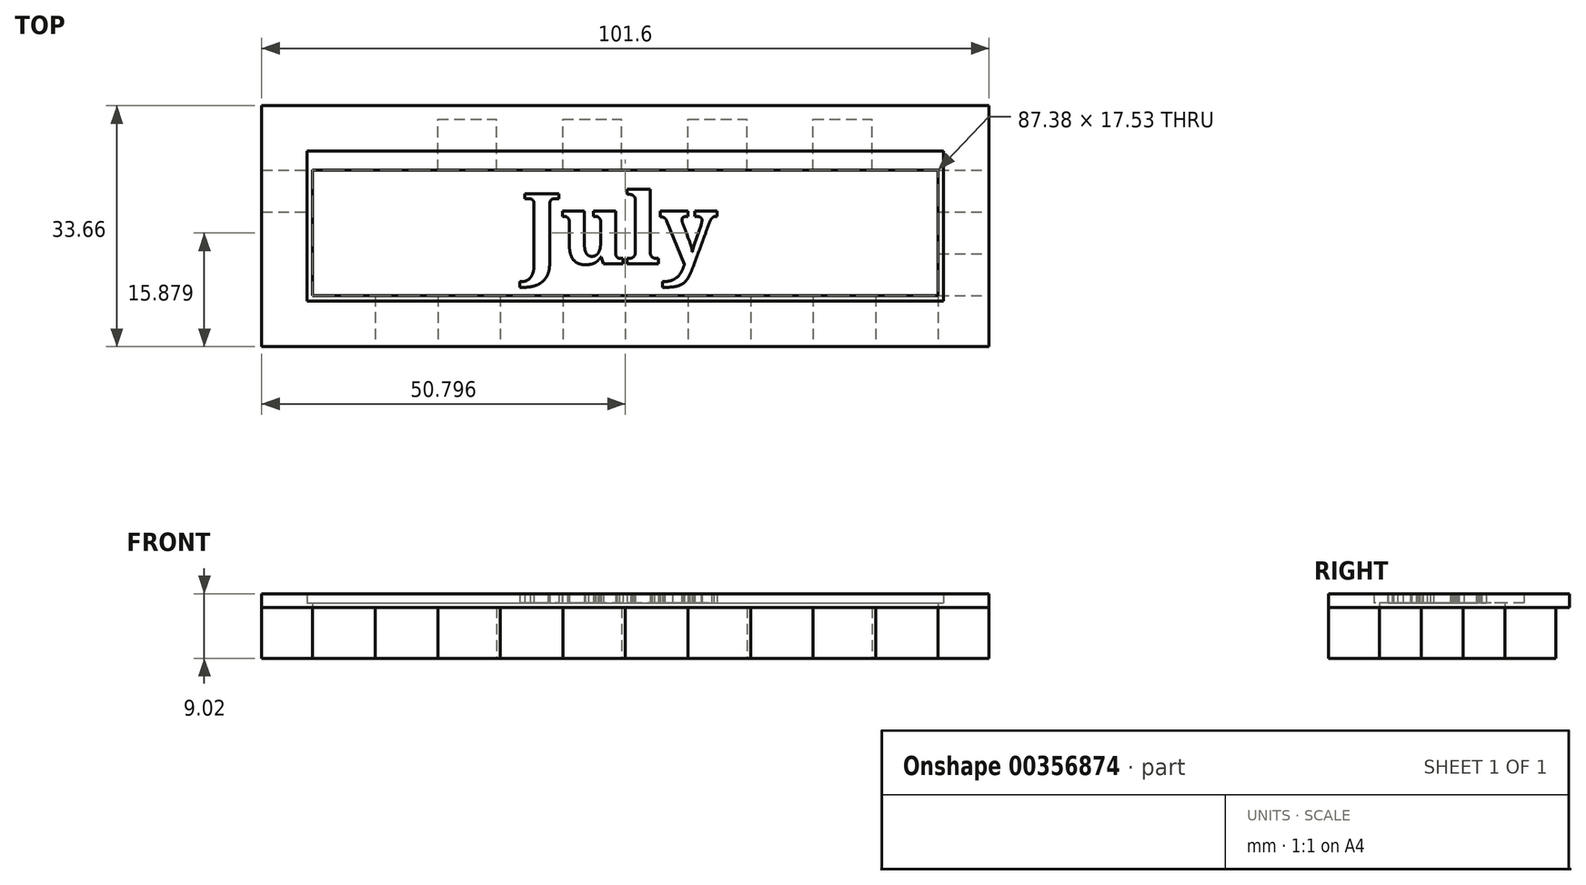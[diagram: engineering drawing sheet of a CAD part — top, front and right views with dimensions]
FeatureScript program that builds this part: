
annotation { "Feature Type Name" : "Feature", "Feature Type Description" : "" }
export const myFeature = defineFeature(function(context is Context, id is Id, definition is map)
    precondition{}
    {
        {
            var Q0;
            Q0=qCreatedBy(makeId("Top.planeOp"),FACE);
            var sketch = newSketch(context, id + "F0", { "sketchPlane" : qUnion([Q0])});
            skLineSegment(sketch, "E0.bottom", {"start": v(-52.12, 11.37) * mm, "end": v(49.48, 11.37) * mm});
            skLineSegment(sketch, "E0.top", {"start": v(-52.12, -20.38) * mm, "end": v(49.48, -20.38) * mm});
            skLineSegment(sketch, "E0.left", {"start": v(-52.12, 11.37) * mm, "end": v(-52.12, -20.38) * mm});
            skLineSegment(sketch, "E0.right", {"start": v(49.48, 11.37) * mm, "end": v(49.48, -20.38) * mm});
            skLineSegment(sketch, "E1.bottom", {"start": v(-52.12, 11.37) * mm, "end": v(-45.01, 11.37) * mm});
            skLineSegment(sketch, "E1.top", {"start": v(-52.12, 4.26) * mm, "end": v(-45.01, 4.26) * mm});
            skLineSegment(sketch, "E1.left", {"start": v(-52.12, 11.37) * mm, "end": v(-52.12, 4.26) * mm});
            skLineSegment(sketch, "E1.right", {"start": v(-45.01, 11.37) * mm, "end": v(-45.01, 4.26) * mm});
            skLineSegment(sketch, "E2.bottom", {"start": v(-45.01, 11.37) * mm, "end": v(-36.78, 11.37) * mm});
            skLineSegment(sketch, "E2.top", {"start": v(-45.01, 4.26) * mm, "end": v(-36.78, 4.26) * mm});
            skLineSegment(sketch, "E2.right", {"start": v(-36.78, 11.37) * mm, "end": v(-36.78, 4.26) * mm});
            skLineSegment(sketch, "E3.bottom", {"start": v(-36.78, 4.26) * mm, "end": v(-27.54, 4.26) * mm});
            skLineSegment(sketch, "E3.top", {"start": v(-36.78, 11.37) * mm, "end": v(-27.54, 11.37) * mm});
            skLineSegment(sketch, "E3.left", {"start": v(-36.78, 4.26) * mm, "end": v(-36.78, 11.37) * mm});
            skLineSegment(sketch, "E3.right", {"start": v(-27.54, 4.26) * mm, "end": v(-27.54, 11.37) * mm});
            skLineSegment(sketch, "E4.bottom", {"start": v(-27.54, 4.26) * mm, "end": v(-19.3, 4.26) * mm});
            skLineSegment(sketch, "E4.top", {"start": v(-27.54, 11.37) * mm, "end": v(-19.3, 11.37) * mm});
            skLineSegment(sketch, "E4.right", {"start": v(-19.3, 4.26) * mm, "end": v(-19.3, 11.37) * mm});
            skLineSegment(sketch, "E5.bottom", {"start": v(-19.3, 4.26) * mm, "end": v(-10.06, 4.26) * mm});
            skLineSegment(sketch, "E5.top", {"start": v(-19.3, 11.37) * mm, "end": v(-10.06, 11.37) * mm});
            skLineSegment(sketch, "E5.right", {"start": v(-10.06, 4.26) * mm, "end": v(-10.06, 11.37) * mm});
            skLineSegment(sketch, "E6.bottom", {"start": v(-10.06, 4.26) * mm, "end": v(-10.06, 4.26) * mm});
            skLineSegment(sketch, "E6.top", {"start": v(-10.06, 11.37) * mm, "end": v(-10.06, 11.37) * mm});
            skLineSegment(sketch, "E7.bottom", {"start": v(-10.06, 4.26) * mm, "end": v(-1.83, 4.26) * mm});
            skLineSegment(sketch, "E7.top", {"start": v(-10.06, 11.37) * mm, "end": v(-1.83, 11.37) * mm});
            skLineSegment(sketch, "E7.right", {"start": v(-1.83, 4.26) * mm, "end": v(-1.83, 11.37) * mm});
            skLineSegment(sketch, "E8.bottom", {"start": v(-1.83, 4.26) * mm, "end": v(7.41, 4.26) * mm});
            skLineSegment(sketch, "E8.top", {"start": v(-1.83, 11.37) * mm, "end": v(7.41, 11.37) * mm});
            skLineSegment(sketch, "E8.right", {"start": v(7.41, 4.26) * mm, "end": v(7.41, 11.37) * mm});
            skLineSegment(sketch, "E9.bottom", {"start": v(7.41, 4.26) * mm, "end": v(15.64, 4.26) * mm});
            skLineSegment(sketch, "E9.top", {"start": v(7.41, 11.37) * mm, "end": v(15.64, 11.37) * mm});
            skLineSegment(sketch, "E9.right", {"start": v(15.64, 4.26) * mm, "end": v(15.64, 11.37) * mm});
            skLineSegment(sketch, "E10.bottom", {"start": v(15.64, 4.26) * mm, "end": v(24.89, 4.26) * mm});
            skLineSegment(sketch, "E10.top", {"start": v(15.64, 11.37) * mm, "end": v(24.89, 11.37) * mm});
            skLineSegment(sketch, "E10.right", {"start": v(24.89, 4.26) * mm, "end": v(24.89, 11.37) * mm});
            skLineSegment(sketch, "E11.bottom", {"start": v(24.89, 4.26) * mm, "end": v(24.89, 4.26) * mm});
            skLineSegment(sketch, "E11.top", {"start": v(24.89, 11.37) * mm, "end": v(24.89, 11.37) * mm});
            skLineSegment(sketch, "E12.bottom", {"start": v(24.89, 4.26) * mm, "end": v(33.12, 4.26) * mm});
            skLineSegment(sketch, "E12.top", {"start": v(24.89, 11.37) * mm, "end": v(33.12, 11.37) * mm});
            skLineSegment(sketch, "E12.right", {"start": v(33.12, 4.26) * mm, "end": v(33.12, 11.37) * mm});
            skLineSegment(sketch, "E13.bottom", {"start": v(33.12, 4.26) * mm, "end": v(42.36, 4.26) * mm});
            skLineSegment(sketch, "E13.top", {"start": v(33.12, 11.37) * mm, "end": v(42.36, 11.37) * mm});
            skLineSegment(sketch, "E13.right", {"start": v(42.36, 4.26) * mm, "end": v(42.36, 11.37) * mm});
            skLineSegment(sketch, "E14.bottom", {"start": v(42.36, 4.26) * mm, "end": v(49.48, 4.26) * mm});
            skLineSegment(sketch, "E14.top", {"start": v(42.36, 11.37) * mm, "end": v(49.48, 11.37) * mm});
            skLineSegment(sketch, "E14.right", {"start": v(49.48, 4.26) * mm, "end": v(49.48, 11.37) * mm});
            skLineSegment(sketch, "E15.bottom", {"start": v(-52.12, -20.38) * mm, "end": v(-45.01, -20.38) * mm});
            skLineSegment(sketch, "E15.top", {"start": v(-52.12, -13.26) * mm, "end": v(-45.01, -13.26) * mm});
            skLineSegment(sketch, "E15.left", {"start": v(-52.12, -20.38) * mm, "end": v(-52.12, -13.26) * mm});
            skLineSegment(sketch, "E15.right", {"start": v(-45.01, -20.38) * mm, "end": v(-45.01, -13.26) * mm});
            skLineSegment(sketch, "E16.bottom", {"start": v(-45.01, -13.26) * mm, "end": v(-45.01, -13.26) * mm});
            skLineSegment(sketch, "E16.top", {"start": v(-45.01, -20.38) * mm, "end": v(-45.01, -20.38) * mm});
            skLineSegment(sketch, "E16.left", {"start": v(-45.01, -13.26) * mm, "end": v(-45.01, -20.38) * mm});
            skLineSegment(sketch, "E16.right", {"start": v(-45.01, -13.26) * mm, "end": v(-45.01, -20.38) * mm});
            skLineSegment(sketch, "E17.bottom", {"start": v(-45.01, -13.26) * mm, "end": v(-36.27, -13.26) * mm});
            skLineSegment(sketch, "E17.top", {"start": v(-45.01, -20.38) * mm, "end": v(-36.27, -20.38) * mm});
            skLineSegment(sketch, "E17.right", {"start": v(-36.27, -13.26) * mm, "end": v(-36.27, -20.38) * mm});
            skLineSegment(sketch, "E18.bottom", {"start": v(-36.27, -13.26) * mm, "end": v(-36.27, -13.26) * mm});
            skLineSegment(sketch, "E18.top", {"start": v(-36.27, -20.38) * mm, "end": v(-36.27, -20.38) * mm});
            skLineSegment(sketch, "E19.bottom", {"start": v(-36.27, -13.26) * mm, "end": v(-27.54, -13.26) * mm});
            skLineSegment(sketch, "E19.top", {"start": v(-36.27, -20.38) * mm, "end": v(-27.54, -20.38) * mm});
            skLineSegment(sketch, "E19.right", {"start": v(-27.54, -13.26) * mm, "end": v(-27.54, -20.38) * mm});
            skLineSegment(sketch, "E20.bottom", {"start": v(-27.54, -13.26) * mm, "end": v(-18.8, -13.26) * mm});
            skLineSegment(sketch, "E20.top", {"start": v(-27.54, -20.38) * mm, "end": v(-18.8, -20.38) * mm});
            skLineSegment(sketch, "E20.right", {"start": v(-18.8, -13.26) * mm, "end": v(-18.8, -20.38) * mm});
            skLineSegment(sketch, "E21.bottom", {"start": v(-18.8, -13.26) * mm, "end": v(-10.06, -13.26) * mm});
            skLineSegment(sketch, "E21.top", {"start": v(-18.8, -20.38) * mm, "end": v(-10.06, -20.38) * mm});
            skLineSegment(sketch, "E21.right", {"start": v(-10.06, -13.26) * mm, "end": v(-10.06, -20.38) * mm});
            skLineSegment(sketch, "E22.bottom", {"start": v(-10.06, -13.26) * mm, "end": v(-1.32, -13.26) * mm});
            skLineSegment(sketch, "E22.top", {"start": v(-10.06, -20.38) * mm, "end": v(-1.32, -20.38) * mm});
            skLineSegment(sketch, "E22.right", {"start": v(-1.32, -13.26) * mm, "end": v(-1.32, -20.38) * mm});
            skLineSegment(sketch, "E23.bottom", {"start": v(-1.32, -13.26) * mm, "end": v(7.41, -13.26) * mm});
            skLineSegment(sketch, "E23.top", {"start": v(-1.32, -20.38) * mm, "end": v(7.41, -20.38) * mm});
            skLineSegment(sketch, "E23.right", {"start": v(7.41, -13.26) * mm, "end": v(7.41, -20.38) * mm});
            skLineSegment(sketch, "E24.bottom", {"start": v(7.41, -13.26) * mm, "end": v(16.15, -13.26) * mm});
            skLineSegment(sketch, "E24.top", {"start": v(7.41, -20.38) * mm, "end": v(16.15, -20.38) * mm});
            skLineSegment(sketch, "E24.right", {"start": v(16.15, -13.26) * mm, "end": v(16.15, -20.38) * mm});
            skLineSegment(sketch, "E25.bottom", {"start": v(16.15, -13.26) * mm, "end": v(24.89, -13.26) * mm});
            skLineSegment(sketch, "E25.top", {"start": v(16.15, -20.38) * mm, "end": v(24.89, -20.38) * mm});
            skLineSegment(sketch, "E25.right", {"start": v(24.89, -13.26) * mm, "end": v(24.89, -20.38) * mm});
            skLineSegment(sketch, "E26.bottom", {"start": v(24.89, -13.26) * mm, "end": v(33.63, -13.26) * mm});
            skLineSegment(sketch, "E26.top", {"start": v(24.89, -20.38) * mm, "end": v(33.63, -20.38) * mm});
            skLineSegment(sketch, "E26.right", {"start": v(33.63, -13.26) * mm, "end": v(33.63, -20.38) * mm});
            skLineSegment(sketch, "E27.bottom", {"start": v(33.63, -13.26) * mm, "end": v(42.36, -13.26) * mm});
            skLineSegment(sketch, "E27.top", {"start": v(33.63, -20.38) * mm, "end": v(42.36, -20.38) * mm});
            skLineSegment(sketch, "E27.right", {"start": v(42.36, -13.26) * mm, "end": v(42.36, -20.38) * mm});
            skLineSegment(sketch, "E28.bottom", {"start": v(42.36, -13.26) * mm, "end": v(49.48, -13.26) * mm});
            skLineSegment(sketch, "E28.top", {"start": v(42.36, -20.38) * mm, "end": v(49.48, -20.38) * mm});
            skLineSegment(sketch, "E28.right", {"start": v(49.48, -13.26) * mm, "end": v(49.48, -20.38) * mm});
            skLineSegment(sketch, "E29.top", {"start": v(-52.12, -1.58) * mm, "end": v(-45.01, -1.58) * mm});
            skLineSegment(sketch, "E29.left", {"start": v(-52.12, 4.26) * mm, "end": v(-52.12, -1.58) * mm});
            skLineSegment(sketch, "E29.right", {"start": v(-45.01, 4.26) * mm, "end": v(-45.01, -1.58) * mm});
            skLineSegment(sketch, "E30.top", {"start": v(-52.12, -7.42) * mm, "end": v(-45.01, -7.42) * mm});
            skLineSegment(sketch, "E30.left", {"start": v(-52.12, -1.58) * mm, "end": v(-52.12, -7.42) * mm});
            skLineSegment(sketch, "E30.right", {"start": v(-45.01, -1.58) * mm, "end": v(-45.01, -7.42) * mm});
            skLineSegment(sketch, "E31.bottom", {"start": v(-45.01, -7.42) * mm, "end": v(-52.12, -7.42) * mm});
            skLineSegment(sketch, "E31.top", {"start": v(-45.01, -13.26) * mm, "end": v(-52.12, -13.26) * mm});
            skLineSegment(sketch, "E31.left", {"start": v(-45.01, -7.42) * mm, "end": v(-45.01, -13.26) * mm});
            skLineSegment(sketch, "E31.right", {"start": v(-52.12, -7.42) * mm, "end": v(-52.12, -13.26) * mm});
            skLineSegment(sketch, "E32.top", {"start": v(42.36, -1.58) * mm, "end": v(49.48, -1.58) * mm});
            skLineSegment(sketch, "E32.left", {"start": v(42.36, 4.26) * mm, "end": v(42.36, -1.58) * mm});
            skLineSegment(sketch, "E32.right", {"start": v(49.48, 4.26) * mm, "end": v(49.48, -1.58) * mm});
            skLineSegment(sketch, "E33.top", {"start": v(42.36, -7.42) * mm, "end": v(49.48, -7.42) * mm});
            skLineSegment(sketch, "E33.left", {"start": v(42.36, -1.58) * mm, "end": v(42.36, -7.42) * mm});
            skLineSegment(sketch, "E33.right", {"start": v(49.48, -1.58) * mm, "end": v(49.48, -7.42) * mm});
            skLineSegment(sketch, "E34.left", {"start": v(42.36, -7.42) * mm, "end": v(42.36, -13.26) * mm});
            skLineSegment(sketch, "E34.right", {"start": v(49.48, -7.42) * mm, "end": v(49.48, -13.26) * mm});
            skSolve(sketch);
        }
        {
            var Q0;
            Q0=makeQuery(id+"F0.imprint","IMPRINT",FACE,{"disambiguationData":[TD([[makeQuery(id+"F0.imprint","IMPRINT",EDGE,{"derivedFrom":sQuery(id+"F0.wireOp",EDGE,"E2.top")}),-1.0]])]});
            var Q1;
            Q1=makeQuery(id+"F0.imprint","IMPRINT",FACE,{"disambiguationData":[TD([[makeQuery(id+"F0.imprint","IMPRINT",EDGE,{"derivedFrom":sQuery(id+"F0.wireOp",EDGE,"E2.bottom")}),-1.0]])]});
            var Q2;
            Q2=makeQuery(id+"F0.imprint","IMPRINT",FACE,{"disambiguationData":[TD([[makeQuery(id+"F0.imprint","IMPRINT",EDGE,{"derivedFrom":sQuery(id+"F0.wireOp",EDGE,"E4.bottom")}),1.0]])]});
            var Q3;
            Q3=makeQuery(id+"F0.imprint","IMPRINT",FACE,{"disambiguationData":[TD([[makeQuery(id+"F0.imprint","IMPRINT",EDGE,{"derivedFrom":sQuery(id+"F0.wireOp",EDGE,"E7.bottom")}),1.0]])]});
            var Q4;
            Q4=makeQuery(id+"F0.imprint","IMPRINT",FACE,{"disambiguationData":[TD([[makeQuery(id+"F0.imprint","IMPRINT",EDGE,{"derivedFrom":sQuery(id+"F0.wireOp",EDGE,"E9.bottom")}),1.0]])]});
            var Q5;
            Q5=makeQuery(id+"F0.imprint","IMPRINT",FACE,{"disambiguationData":[TD([[makeQuery(id+"F0.imprint","IMPRINT",EDGE,{"derivedFrom":sQuery(id+"F0.wireOp",EDGE,"E12.bottom")}),1.0]])]});
            var Q6;
            Q6=makeQuery(id+"F0.imprint","IMPRINT",FACE,{"disambiguationData":[TD([[makeQuery(id+"F0.imprint","IMPRINT",EDGE,{"derivedFrom":sQuery(id+"F0.wireOp",EDGE,"E14.bottom")}),-1.0]])]});
            var Q7;
            Q7=makeQuery(id+"F0.imprint","IMPRINT",FACE,{"disambiguationData":[TD([[makeQuery(id+"F0.imprint","IMPRINT",EDGE,{"derivedFrom":sQuery(id+"F0.wireOp",EDGE,"E33.top")}),-1.0]])]});
            var Q8;
            Q8=makeQuery(id+"F0.imprint","IMPRINT",FACE,{"disambiguationData":[TD([[makeQuery(id+"F0.imprint","IMPRINT",EDGE,{"derivedFrom":sQuery(id+"F0.wireOp",EDGE,"E27.bottom")}),-1.0]])]});
            var Q9;
            Q9=makeQuery(id+"F0.imprint","IMPRINT",FACE,{"disambiguationData":[TD([[makeQuery(id+"F0.imprint","IMPRINT",EDGE,{"derivedFrom":sQuery(id+"F0.wireOp",EDGE,"E25.bottom")}),-1.0]])]});
            var Q10;
            Q10=makeQuery(id+"F0.imprint","IMPRINT",FACE,{"disambiguationData":[TD([[makeQuery(id+"F0.imprint","IMPRINT",EDGE,{"derivedFrom":sQuery(id+"F0.wireOp",EDGE,"E23.bottom")}),-1.0]])]});
            var Q11;
            Q11=makeQuery(id+"F0.imprint","IMPRINT",FACE,{"disambiguationData":[TD([[makeQuery(id+"F0.imprint","IMPRINT",EDGE,{"derivedFrom":sQuery(id+"F0.wireOp",EDGE,"E21.bottom")}),-1.0]])]});
            var Q12;
            Q12=makeQuery(id+"F0.imprint","IMPRINT",FACE,{"disambiguationData":[TD([[makeQuery(id+"F0.imprint","IMPRINT",EDGE,{"derivedFrom":sQuery(id+"F0.wireOp",EDGE,"E19.bottom")}),-1.0]])]});
            var Q13;
            Q13=makeQuery(id+"F0.imprint","IMPRINT",FACE,{"disambiguationData":[TD([[makeQuery(id+"F0.imprint","IMPRINT",EDGE,{"derivedFrom":sQuery(id+"F0.wireOp",EDGE,"E31.bottom")}),1.0]])]});
            var Q14;
            Q14=makeQuery(id+"F0.imprint","IMPRINT",FACE,{"disambiguationData":[TD([[makeQuery(id+"F0.imprint","IMPRINT",EDGE,{"derivedFrom":sQuery(id+"F0.wireOp",EDGE,"E1.top")}),-1.0]])]});
            extrude(context, id + "F1", {"entities" : qUnion([Q0, Q1, Q2, Q3, Q4, Q5, Q6, Q7, Q8, Q9, Q10, Q11, Q12, Q13, Q14]), "depth" : 7.11 * mm});
        }
        {
            var Q0;
            Q0=makeQuery(id+"F1.opExtrude","CAP_FACE",FACE,{"disambiguationData":[OSD([sQuery(id+"F0.wireOp",EDGE,"E2.bottom"),sQuery(id+"F0.wireOp",EDGE,"E1.right"),sQuery(id+"F0.wireOp",EDGE,"E3.bottom"),sQuery(id+"F0.wireOp",EDGE,"E3.left"),sQuery(id+"F0.wireOp",EDGE,"E4.top"),sQuery(id+"F0.wireOp",EDGE,"E3.right"),sQuery(id+"F0.wireOp",EDGE,"E5.bottom"),sQuery(id+"F0.wireOp",EDGE,"E4.right"),sQuery(id+"F0.wireOp",EDGE,"E6.top"),sQuery(id+"F0.wireOp",EDGE,"E5.right"),sQuery(id+"F0.wireOp",EDGE,"E7.bottom"),sQuery(id+"F0.wireOp",EDGE,"E5.right"),sQuery(id+"F0.wireOp",EDGE,"E8.top"),sQuery(id+"F0.wireOp",EDGE,"E7.right"),sQuery(id+"F0.wireOp",EDGE,"E9.bottom"),sQuery(id+"F0.wireOp",EDGE,"E8.right"),sQuery(id+"F0.wireOp",EDGE,"E10.top"),sQuery(id+"F0.wireOp",EDGE,"E9.right"),sQuery(id+"F0.wireOp",EDGE,"E11.bottom"),sQuery(id+"F0.wireOp",EDGE,"E10.right"),sQuery(id+"F0.wireOp",EDGE,"E12.top"),sQuery(id+"F0.wireOp",EDGE,"E10.right"),sQuery(id+"F0.wireOp",EDGE,"E13.bottom"),sQuery(id+"F0.wireOp",EDGE,"E12.right"),sQuery(id+"F0.wireOp",EDGE,"E16.bottom"),sQuery(id+"F0.wireOp",EDGE,"E17.top"),sQuery(id+"F0.wireOp",EDGE,"E16.left"),sQuery(id+"F0.wireOp",EDGE,"E18.bottom"),sQuery(id+"F0.wireOp",EDGE,"E17.right"),sQuery(id+"F0.wireOp",EDGE,"E19.top"),sQuery(id+"F0.wireOp",EDGE,"E17.right"),sQuery(id+"F0.wireOp",EDGE,"E20.bottom"),sQuery(id+"F0.wireOp",EDGE,"E19.right"),sQuery(id+"F0.wireOp",EDGE,"E21.top"),sQuery(id+"F0.wireOp",EDGE,"E20.right"),sQuery(id+"F0.wireOp",EDGE,"E22.bottom"),sQuery(id+"F0.wireOp",EDGE,"E21.right"),sQuery(id+"F0.wireOp",EDGE,"E23.top"),sQuery(id+"F0.wireOp",EDGE,"E22.right"),sQuery(id+"F0.wireOp",EDGE,"E24.bottom"),sQuery(id+"F0.wireOp",EDGE,"E23.right"),sQuery(id+"F0.wireOp",EDGE,"E25.top"),sQuery(id+"F0.wireOp",EDGE,"E24.right"),sQuery(id+"F0.wireOp",EDGE,"E26.bottom"),sQuery(id+"F0.wireOp",EDGE,"E25.right"),sQuery(id+"F0.wireOp",EDGE,"E27.top"),sQuery(id+"F0.wireOp",EDGE,"E26.right"),sQuery(id+"F0.wireOp",EDGE,"E27.right"),sQuery(id+"F0.wireOp",EDGE,"E1.top"),sQuery(id+"F0.wireOp",EDGE,"E29.left"),sQuery(id+"F0.wireOp",EDGE,"E29.top"),sQuery(id+"F0.wireOp",EDGE,"E30.right"),sQuery(id+"F0.wireOp",EDGE,"E31.bottom"),sQuery(id+"F0.wireOp",EDGE,"E31.top"),sQuery(id+"F0.wireOp",EDGE,"E31.right"),sQuery(id+"F0.wireOp",EDGE,"E14.bottom"),sQuery(id+"F0.wireOp",EDGE,"E32.right"),sQuery(id+"F0.wireOp",EDGE,"E32.top"),sQuery(id+"F0.wireOp",EDGE,"E33.left"),sQuery(id+"F0.wireOp",EDGE,"E33.top"),sQuery(id+"F0.wireOp",EDGE,"E28.bottom"),sQuery(id+"F0.wireOp",EDGE,"E34.right")])],"isStart":false});
            var sketch = newSketch(context, id + "F2", { "sketchPlane" : qUnion([Q0])});
            skLineSegment(sketch, "E35.bottom", {"start": v(-52.12, -20.38) * mm, "end": v(-45.01, -20.38) * mm});
            skLineSegment(sketch, "E35.top", {"start": v(-52.12, 13.28) * mm, "end": v(-45.01, 13.28) * mm});
            skLineSegment(sketch, "E35.left", {"start": v(-52.12, -20.38) * mm, "end": v(-52.12, 13.28) * mm});
            skLineSegment(sketch, "E35.right", {"start": v(-45.01, -20.38) * mm, "end": v(-45.01, 13.28) * mm});
            skLineSegment(sketch, "E36.bottom", {"start": v(-52.12, -20.38) * mm, "end": v(49.48, -20.38) * mm});
            skLineSegment(sketch, "E36.top", {"start": v(-52.12, -13.26) * mm, "end": v(49.48, -13.26) * mm});
            skLineSegment(sketch, "E36.left", {"start": v(-52.12, -20.38) * mm, "end": v(-52.12, -13.26) * mm});
            skLineSegment(sketch, "E36.right", {"start": v(49.48, -20.38) * mm, "end": v(49.48, -13.26) * mm});
            skPoint(sketch, "E37.oppositeSnap0", {"position": v(42.36, -4.5) * mm});
            skLineSegment(sketch, "E37.bottom", {"start": v(49.48, -20.38) * mm, "end": v(42.36, -20.38) * mm});
            skLineSegment(sketch, "E37.top", {"start": v(49.48, 13.28) * mm, "end": v(42.36, 13.28) * mm});
            skLineSegment(sketch, "E37.left", {"start": v(49.48, -20.38) * mm, "end": v(49.48, 13.28) * mm});
            skLineSegment(sketch, "E37.right", {"start": v(42.36, -20.38) * mm, "end": v(42.36, 13.28) * mm});
            skLineSegment(sketch, "E38.bottom", {"start": v(-52.12, 13.28) * mm, "end": v(49.48, 13.28) * mm});
            skLineSegment(sketch, "E38.top", {"start": v(-52.12, 4.26) * mm, "end": v(49.48, 4.26) * mm});
            skLineSegment(sketch, "E38.left", {"start": v(-52.12, 13.28) * mm, "end": v(-52.12, 4.26) * mm});
            skLineSegment(sketch, "E38.right", {"start": v(49.48, 13.28) * mm, "end": v(49.48, 4.26) * mm});
            skSolve(sketch);
        }
        {
            var Q0;
            Q0=qSketchRegion(id+"F2",true);
            var Q1;
            {var subQ5=sQuery(id+"F2.wireOp",EDGE,"E36.top");var subQ10=sQuery(id+"F2.wireOp",EDGE,"E35.right");var subQ12=makeQuery(id+"F2.imprint","INTERSECT",VERTEX,{"derivedFrom":[makeQuery(id+"F1.opExtrude","CAP_EDGE",EDGE,{"disambiguationData":[OSD([sQuery(id+"F0.wireOp",EDGE,"E31.bottom")])],"isStart":false}),subQ10]});var subQ24=makeQuery(id+"F2.imprint","INTERSECT",VERTEX,{"derivedFrom":[subQ10,subQ5]});Q1=makeQuery(id+"F2.imprint","IMPRINT",FACE,{"disambiguationData":[TD([[makeQuery(id+"F2.imprint","IMPRINT",EDGE,{"disambiguationData":[TD([[subQ12,1.0],[subQ24,-1.0]])],"derivedFrom":subQ10}),-1.0]])]});}
            extrude(context, id + "F3", {"entities" : qUnion([Q0, Q1]), "depth" : 0.64 * mm});
        }
        {
            var Q0;
            Q0=makeQuery(id+"F3.opExtrude","CAP_FACE",FACE,{"disambiguationData":[OSD([sQuery(id+"F2.wireOp",EDGE,"E35.left"),sQuery(id+"F2.wireOp",EDGE,"E36.bottom"),sQuery(id+"F2.wireOp",EDGE,"E36.left"),sQuery(id+"F2.wireOp",EDGE,"E37.bottom"),sQuery(id+"F2.wireOp",EDGE,"E37.left"),sQuery(id+"F2.wireOp",EDGE,"E38.bottom"),sQuery(id+"F2.wireOp",EDGE,"E38.left"),sQuery(id+"F2.wireOp",EDGE,"E38.right")])],"isStart":false});
            var sketch = newSketch(context, id + "F4", { "sketchPlane" : qUnion([Q0])});
            skLineSegment(sketch, "E39.bottom", {"start": v(-52.12, 13.28) * mm, "end": v(49.48, 13.28) * mm});
            skLineSegment(sketch, "E39.top", {"start": v(-52.12, 6.93) * mm, "end": v(49.48, 6.93) * mm});
            skLineSegment(sketch, "E39.left", {"start": v(-52.12, 13.28) * mm, "end": v(-52.12, 6.93) * mm});
            skLineSegment(sketch, "E39.right", {"start": v(49.48, 13.28) * mm, "end": v(49.48, 6.93) * mm});
            skLineSegment(sketch, "E40.bottom", {"start": v(-52.12, 13.28) * mm, "end": v(-45.77, 13.28) * mm});
            skLineSegment(sketch, "E40.top", {"start": v(-52.12, -20.38) * mm, "end": v(-45.77, -20.38) * mm});
            skLineSegment(sketch, "E40.left", {"start": v(-52.12, 13.28) * mm, "end": v(-52.12, -20.38) * mm});
            skLineSegment(sketch, "E40.right", {"start": v(-45.77, 13.28) * mm, "end": v(-45.77, -20.38) * mm});
            skLineSegment(sketch, "E41.bottom", {"start": v(-52.12, -14.03) * mm, "end": v(49.48, -14.03) * mm});
            skLineSegment(sketch, "E41.top", {"start": v(-52.12, -20.38) * mm, "end": v(49.48, -20.38) * mm});
            skLineSegment(sketch, "E41.left", {"start": v(-52.12, -14.03) * mm, "end": v(-52.12, -20.38) * mm});
            skLineSegment(sketch, "E41.right", {"start": v(49.48, -14.03) * mm, "end": v(49.48, -20.38) * mm});
            skLineSegment(sketch, "E42.bottom", {"start": v(49.48, -20.38) * mm, "end": v(43.13, -20.38) * mm});
            skLineSegment(sketch, "E42.top", {"start": v(49.48, 13.28) * mm, "end": v(43.13, 13.28) * mm});
            skLineSegment(sketch, "E42.left", {"start": v(49.48, -20.38) * mm, "end": v(49.48, 13.28) * mm});
            skLineSegment(sketch, "E42.right", {"start": v(43.13, -20.38) * mm, "end": v(43.13, 13.28) * mm});
            skSolve(sketch);
        }
        {
            var Q0;
            Q0=qSketchRegion(id+"F4",true);
            extrude(context, id + "F5", {"entities" : qUnion([Q0]), "operationType" : NewBodyOperationType.ADD, "depth" : 1.27 * mm});
        }
        {
            var Q0;
            Q0=makeQuery(id+"F3.opExtrude","CAP_FACE",FACE,{"disambiguationData":[OSD([sQuery(id+"F2.wireOp",EDGE,"E35.left"),sQuery(id+"F2.wireOp",EDGE,"E36.bottom"),sQuery(id+"F2.wireOp",EDGE,"E36.left"),sQuery(id+"F2.wireOp",EDGE,"E37.bottom"),sQuery(id+"F2.wireOp",EDGE,"E37.left"),sQuery(id+"F2.wireOp",EDGE,"E38.bottom"),sQuery(id+"F2.wireOp",EDGE,"E38.left"),sQuery(id+"F2.wireOp",EDGE,"E38.right")])],"isStart":false});
            var sketch = newSketch(context, id + "F6", { "sketchPlane" : qUnion([Q0])});
            skText(sketch, "E43", { "text": "July", "fontName": "NotoSerif-Bold.ttf"});
            const initialGuessF6  = {"E43": [-0.01552, -0.0088, 1, 0, 0.00988]};
            skSetInitialGuess(sketch, initialGuessF6);
            skSolve(sketch);
        }
        {
            var Q0;
            Q0 = qSketchRegion(id + "F6", true);
            extrude(context, id + "F7", {"entities" : qUnion([Q0]), "operationType" : NewBodyOperationType.ADD, "depth" : 1.27 * mm});
        }
    });
